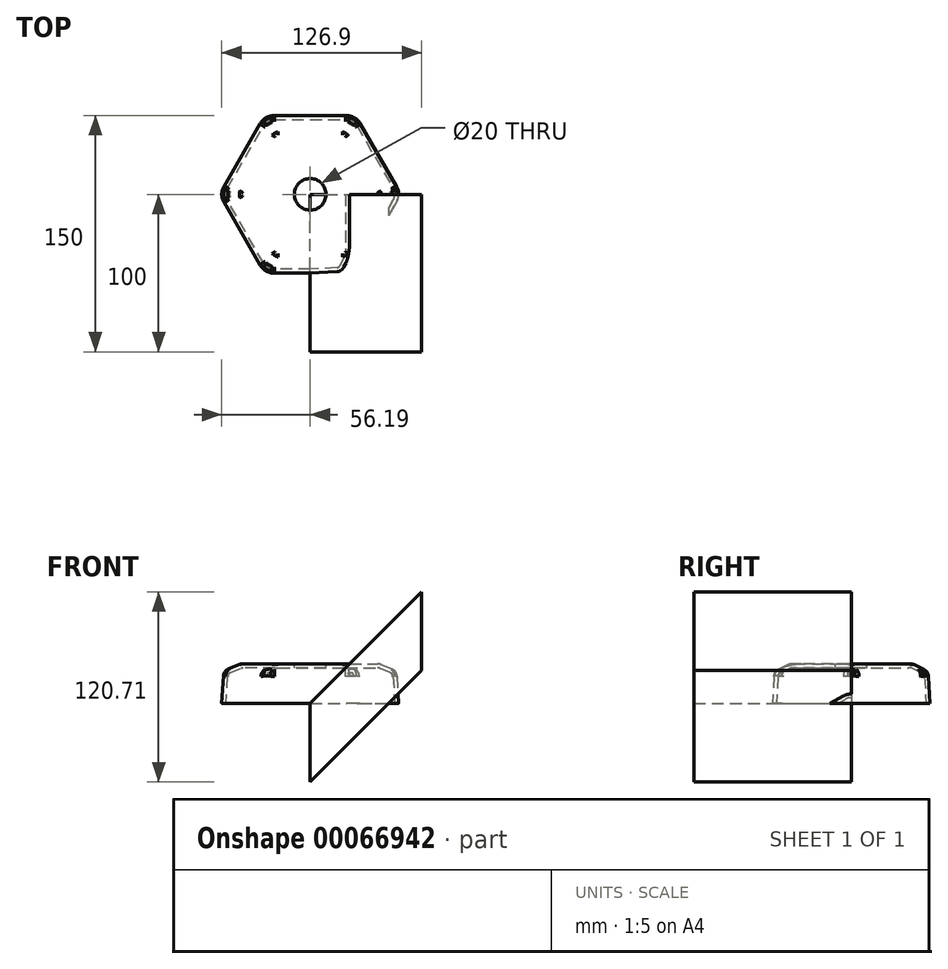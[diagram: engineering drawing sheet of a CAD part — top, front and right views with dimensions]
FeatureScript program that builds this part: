
annotation { "Feature Type Name" : "Feature", "Feature Type Description" : "" }
export const myFeature = defineFeature(function(context is Context, id is Id, definition is map)
    precondition{}
    {
        {
            var Q0;
            Q0=qCreatedBy(makeId("Top.planeOp"),FACE);
            var sketch = newSketch(context, id + "F0", { "sketchPlane" : qUnion([Q0])});
            skCircle(sketch, "E0.cCircle", {"center": v(0, 0) * mm, "radius": 50 * mm, "construction": true});
            skLineSegment(sketch, "E0.0", {"start": v(-28.87, 50) * mm, "end": v(28.87, 50) * mm});
            skLineSegment(sketch, "E0.1", {"start": v(28.87, 50) * mm, "end": v(57.74, 0) * mm});
            skLineSegment(sketch, "E0.2", {"start": v(57.74, 0) * mm, "end": v(28.87, -50) * mm});
            skLineSegment(sketch, "E0.3", {"start": v(28.87, -50) * mm, "end": v(-28.87, -50) * mm});
            skLineSegment(sketch, "E0.4", {"start": v(-28.87, -50) * mm, "end": v(-57.74, 0) * mm});
            skLineSegment(sketch, "E0.5", {"start": v(-57.74, 0) * mm, "end": v(-28.87, 50) * mm});
            skPoint(sketch, "E0.0.midPoint", {"position": v(0, 50) * mm});
            skSolve(sketch);
        }
        {
            var Q0;
            Q0=makeQuery(id+"F0.imprint","IMPRINT",FACE,{"disambiguationData":[TD([[makeQuery(id+"F0.imprint","IMPRINT",EDGE,{"derivedFrom":sQuery(id+"F0.wireOp",EDGE,"E0.0")}),-1.0]])]});
            extrude(context, id + "F1", {"entities" : qUnion([Q0]), "depth" : 25 * mm, "hasDraft" : true, "draftAngle" : 3 * degree, "draftPullDirection" : true});
        }
        {
            var Q0;
            Q0=makeQuery(id+"F1.opExtrude","CAP_FACE",FACE,{"disambiguationData":[OSD([sQuery(id+"F0.wireOp",EDGE,"E0.0"),sQuery(id+"F0.wireOp",EDGE,"E0.1"),sQuery(id+"F0.wireOp",EDGE,"E0.2"),sQuery(id+"F0.wireOp",EDGE,"E0.3"),sQuery(id+"F0.wireOp",EDGE,"E0.4"),sQuery(id+"F0.wireOp",EDGE,"E0.5")])],"isStart":false});
            chamfer(context, id + "F2", {"entities" : qUnion([Q0]), "chamferType" : ChamferType.TWO_OFFSETS, "width1" : 5 * mm, "oppositeDirection" : false, "width2" : 10 * mm, "tangentPropagation" : true});
        }
        {
            var Q0;
            Q0=makeQuery(id+"F2.opChamfer","BLEND_EDGE",EDGE,{"blendedFrom":[makeQuery(id+"F1.opExtrude","CAP_EDGE",EDGE,{"disambiguationData":[OSD([sQuery(id+"F0.wireOp",EDGE,"E0.3")])],"isStart":false}),makeQuery(id+"F1.opExtrude","CAP_EDGE",EDGE,{"disambiguationData":[OSD([sQuery(id+"F0.wireOp",EDGE,"E0.4")])],"isStart":false})],"blendedInto":[]});
            var Q1;
            Q1=makeQuery(id+"F2.opChamfer","BLEND_EDGE",EDGE,{"blendedFrom":[makeQuery(id+"F1.opExtrude","CAP_EDGE",EDGE,{"disambiguationData":[OSD([sQuery(id+"F0.wireOp",EDGE,"E0.2")])],"isStart":false}),makeQuery(id+"F1.opExtrude","CAP_EDGE",EDGE,{"disambiguationData":[OSD([sQuery(id+"F0.wireOp",EDGE,"E0.3")])],"isStart":false})],"blendedInto":[]});
            var Q2;
            Q2=makeQuery(id+"F2.opChamfer","BLEND_EDGE",EDGE,{"blendedFrom":[makeQuery(id+"F1.opExtrude","CAP_EDGE",EDGE,{"disambiguationData":[OSD([sQuery(id+"F0.wireOp",EDGE,"E0.1")])],"isStart":false}),makeQuery(id+"F1.opExtrude","CAP_EDGE",EDGE,{"disambiguationData":[OSD([sQuery(id+"F0.wireOp",EDGE,"E0.2")])],"isStart":false})],"blendedInto":[]});
            var Q3;
            Q3=makeQuery(id+"F2.opChamfer","BLEND_EDGE",EDGE,{"blendedFrom":[makeQuery(id+"F1.opExtrude","CAP_EDGE",EDGE,{"disambiguationData":[OSD([sQuery(id+"F0.wireOp",EDGE,"E0.0")])],"isStart":false}),makeQuery(id+"F1.opExtrude","CAP_EDGE",EDGE,{"disambiguationData":[OSD([sQuery(id+"F0.wireOp",EDGE,"E0.1")])],"isStart":false})],"blendedInto":[]});
            var Q4;
            Q4=makeQuery(id+"F2.opChamfer","BLEND_EDGE",EDGE,{"blendedFrom":[makeQuery(id+"F1.opExtrude","CAP_EDGE",EDGE,{"disambiguationData":[OSD([sQuery(id+"F0.wireOp",EDGE,"E0.0")])],"isStart":false}),makeQuery(id+"F1.opExtrude","CAP_EDGE",EDGE,{"disambiguationData":[OSD([sQuery(id+"F0.wireOp",EDGE,"E0.5")])],"isStart":false})],"blendedInto":[]});
            var Q5;
            Q5=makeQuery(id+"F2.opChamfer","BLEND_EDGE",EDGE,{"blendedFrom":[makeQuery(id+"F1.opExtrude","CAP_EDGE",EDGE,{"disambiguationData":[OSD([sQuery(id+"F0.wireOp",EDGE,"E0.4")])],"isStart":false}),makeQuery(id+"F1.opExtrude","CAP_EDGE",EDGE,{"disambiguationData":[OSD([sQuery(id+"F0.wireOp",EDGE,"E0.5")])],"isStart":false})],"blendedInto":[]});
            var Q6;
            Q6=makeQuery(id+"F1.opExtrude","SWEPT_EDGE",EDGE,{"disambiguationData":[OSD([sQuery(id+"F0.wireOp",EDGE,"E0.4"),sQuery(id+"F0.wireOp",EDGE,"E0.5")])]});
            var Q7;
            Q7=makeQuery(id+"F1.opExtrude","SWEPT_EDGE",EDGE,{"disambiguationData":[OSD([sQuery(id+"F0.wireOp",EDGE,"E0.3"),sQuery(id+"F0.wireOp",EDGE,"E0.4")])]});
            var Q8;
            Q8=makeQuery(id+"F1.opExtrude","SWEPT_EDGE",EDGE,{"disambiguationData":[OSD([sQuery(id+"F0.wireOp",EDGE,"E0.2"),sQuery(id+"F0.wireOp",EDGE,"E0.3")])]});
            var Q9;
            Q9=makeQuery(id+"F1.opExtrude","SWEPT_EDGE",EDGE,{"disambiguationData":[OSD([sQuery(id+"F0.wireOp",EDGE,"E0.1"),sQuery(id+"F0.wireOp",EDGE,"E0.2")])]});
            var Q10;
            Q10=makeQuery(id+"F1.opExtrude","SWEPT_EDGE",EDGE,{"disambiguationData":[OSD([sQuery(id+"F0.wireOp",EDGE,"E0.0"),sQuery(id+"F0.wireOp",EDGE,"E0.5")])]});
            var Q11;
            Q11=makeQuery(id+"F1.opExtrude","SWEPT_EDGE",EDGE,{"disambiguationData":[OSD([sQuery(id+"F0.wireOp",EDGE,"E0.0"),sQuery(id+"F0.wireOp",EDGE,"E0.1")])]});
            fillet(context, id + "F3", {"entities" : qUnion([Q0, Q1, Q2, Q3, Q4, Q5, Q6, Q7, Q8, Q9, Q10, Q11]), "radius" : 10 * mm, "tangentPropagation" : true, "allowEdgeOverflow" : false});
        }
        {
            var Q0;
            {var subQ0=sQuery(id+"F0.wireOp",EDGE,"E0.3");Q0=makeQuery(id+"F2.opChamfer","BLEND_EDGE",EDGE,{"blendedFrom":[makeQuery(id+"F1.opExtrude","CAP_EDGE",EDGE,{"disambiguationData":[OSD([subQ0])],"isStart":false}),makeQuery(id+"F1.opExtrude","SWEPT_FACE",FACE,{"disambiguationData":[OSD([subQ0])]})],"blendedInto":[makeQuery(id+"F1.opExtrude","SWEPT_FACE",FACE,{"disambiguationData":[OSD([subQ0])]})]});}
            var Q1;
            {var subQ0=sQuery(id+"F0.wireOp",EDGE,"E0.3");Q1=makeQuery(id+"F2.opChamfer","BLEND_EDGE",EDGE,{"blendedFrom":[makeQuery(id+"F1.opExtrude","CAP_EDGE",EDGE,{"disambiguationData":[OSD([subQ0])],"isStart":false}),makeQuery(id+"F1.opExtrude","CAP_FACE",FACE,{"disambiguationData":[OSD([sQuery(id+"F0.wireOp",EDGE,"E0.0"),sQuery(id+"F0.wireOp",EDGE,"E0.1"),sQuery(id+"F0.wireOp",EDGE,"E0.2"),subQ0,sQuery(id+"F0.wireOp",EDGE,"E0.4"),sQuery(id+"F0.wireOp",EDGE,"E0.5")])],"isStart":false})],"blendedInto":[makeQuery(id+"F1.opExtrude","CAP_FACE",FACE,{"disambiguationData":[OSD([sQuery(id+"F0.wireOp",EDGE,"E0.0"),sQuery(id+"F0.wireOp",EDGE,"E0.1"),sQuery(id+"F0.wireOp",EDGE,"E0.2"),subQ0,sQuery(id+"F0.wireOp",EDGE,"E0.4"),sQuery(id+"F0.wireOp",EDGE,"E0.5")])],"isStart":false})]});}
            fillet(context, id + "F4", {"entities" : qUnion([Q0, Q1]), "radius" : 5 * mm, "tangentPropagation" : true, "allowEdgeOverflow" : false});
        }
        {
            var Q0;
            Q0=makeQuery(id+"F1.opExtrude","CAP_FACE",FACE,{"disambiguationData":[OSD([sQuery(id+"F0.wireOp",EDGE,"E0.0"),sQuery(id+"F0.wireOp",EDGE,"E0.1"),sQuery(id+"F0.wireOp",EDGE,"E0.2"),sQuery(id+"F0.wireOp",EDGE,"E0.3"),sQuery(id+"F0.wireOp",EDGE,"E0.4"),sQuery(id+"F0.wireOp",EDGE,"E0.5")])],"isStart":true});
            shell(context, id + "F5", {"entities" : qUnion([Q0]), "thickness" : 2.5 * mm});
        }
        {
            var Q0;
            Q0=makeQuery(id+"F1.opExtrude","CAP_FACE",FACE,{"disambiguationData":[OSD([sQuery(id+"F0.wireOp",EDGE,"E0.0"),sQuery(id+"F0.wireOp",EDGE,"E0.1"),sQuery(id+"F0.wireOp",EDGE,"E0.2"),sQuery(id+"F0.wireOp",EDGE,"E0.3"),sQuery(id+"F0.wireOp",EDGE,"E0.4"),sQuery(id+"F0.wireOp",EDGE,"E0.5")])],"isStart":false});
            var sketch = newSketch(context, id + "F6", { "sketchPlane" : qUnion([Q0])});
            skCircle(sketch, "E1", {"center": v(0, 0) * mm, "radius": 10 * mm});
            skSolve(sketch);
        }
        {
            var Q0;
            Q0=makeQuery(id+"F6.imprint","IMPRINT",FACE,{"disambiguationData":[TD([[makeQuery(id+"F6.imprint","IMPRINT",EDGE,{"derivedFrom":sQuery(id+"F6.wireOp",EDGE,"E1")}),1.0]])]});
            extrude(context, id + "F7", {"entities" : qUnion([Q0]), "operationType" : NewBodyOperationType.REMOVE, "endBound" : BoundingType.THROUGH_ALL, "oppositeDirection" : true, "depth" : 25 * mm});
        }
        {
            var Q0;
            Q0=qCreatedBy(makeId("Front.planeOp"),FACE);
            var sketch = newSketch(context, id + "F8", { "sketchPlane" : qUnion([Q0])});
            skLineSegment(sketch, "E2", {"start": v(0, 0) * mm, "end": v(70.71, 70.71) * mm});
            skLineSegment(sketch, "E3", {"start": v(70.71, 70.71) * mm, "end": v(70.71, 20.71) * mm});
            skLineSegment(sketch, "E4", {"start": v(70.71, 20.71) * mm, "end": v(0, -50) * mm});
            skLineSegment(sketch, "E5", {"start": v(0, -50) * mm, "end": v(0, 0) * mm});
            skSolve(sketch);
        }
        {
            var Q0;
            Q0 = qSketchRegion(id + "F8", true);
            extrude(context, id + "F9", {"entities" : qUnion([Q0]), "operationType" : NewBodyOperationType.ADD, "depth" : 100 * mm});
        }
    });
